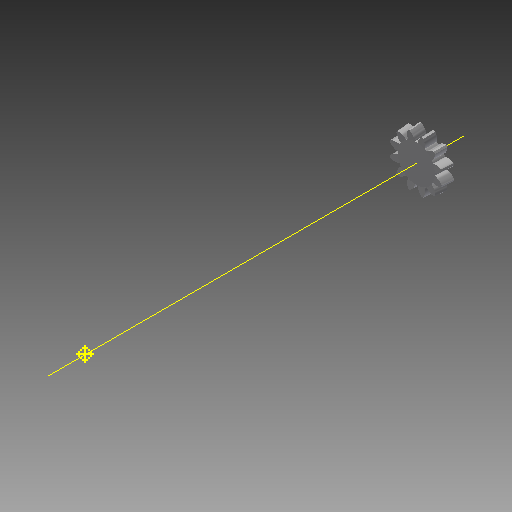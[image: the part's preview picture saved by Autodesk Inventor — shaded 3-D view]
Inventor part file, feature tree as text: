
AUTODESK INVENTOR PART (.ipt)
format: ipt  version: 2017 (Build 210142000, 142)  size: 427,520 bytes
history: native  units: mm
features: other x24, loft x2, pattern_circular x2, sketch x1
ambient origin geometry x6: Origin, XZ Plane, X Axis, Y Axis, Z Axis, Center Point
bodies: Solid1 (feature_tree)
feature tree (29):
  other  "Top Point"
  other  "Mesh Plane2"
  other  "Teeth Body"
  other  "Start Point"
  other  "Tooth Plane"
  other  "Start Sketch"
  other  "End Point"
  other  "3D Sketch Right"
  other  "End Plane Right"
  loft  "Loft Right"
  pattern_circular  "Circular Pattern Right"  [2 undecoded]
  other  "3D Sketch Left"
  other  "End Plane Left"
  loft  "Loft Left"
  pattern_circular  "Circular Pattern Left"  [2 undecoded]
  other  "Fix Body"
  other  "Mesh Plane"
  other  "Top Plane"
  other  "Teeth Body Sketch"
  other  "End Plane"
  other  "End Sketch"
  other  "Helical Curve Left"
  other  "End Sketch Left"
  other  "Body Sketch"
  sketch  "Sketch6"  dims[d0=20.32mm d1=16.687766mm d2=23.785175mm d3=5.08mm d4=148.895202mm d5=90.0deg d7=5.001282mm d8=5.466242mm d9=7.460675mm d11=5.257847mm d12=4.830224mm d15=5.279282mm d16=7.2055mm d17=0.0mm d18=90.0deg d19=0.0mm d20=90.0deg d21=120.0mm d22=360.0deg d26=126.354885mm d27=5.245668mm d28=20.32mm d29=-0.680765mm d30=4.830224mm d31=5.279282mm d32=7.2055mm d35=0.0mm d37=0.0mm d39=0.0mm d40=90.0deg d41=120.0mm d42=360.0deg d46=90.0deg d47=90.0deg d48=0.0mm d49=0.0mm d50=90.0deg d51=15.0deg d52=0.0mm d53=0.0mm d54=0.0mm d56=11.461497mm d57=12.987282mm d58=7.936422mm d59=12.543082mm d60=7.664975mm d61=12.543082mm d62=7.664975mm d63=90.0deg d64=90.0deg d65=126.354885mm d66=31.5mm d67=20.32mm d68=-0.680765mm d69=5.245668mm d70=5.279282mm d71=7.2055mm d72=4.830224mm d73=7.664975mm d74=12.543082mm d75=0.0mm d76=90.0deg d77=0.0mm d78=90.0deg d79=0.0mm d80=90.0deg d81=120.0mm d82=360.0deg d84=10.0mm d85=20.0mm d86=20.0mm d87=10.0mm d88=0.0mm d89=0.0mm]
  other  "Srf1"
  other  "Helical Curve Right"
  other  "End Sketch Right"
  other  "Pitch Diameter"
note: 4 required parameter values undecoded (feature->parameter linkage not recoverable at this tier; creation-order binding heuristic only, values carry confidence <= 0.55)
